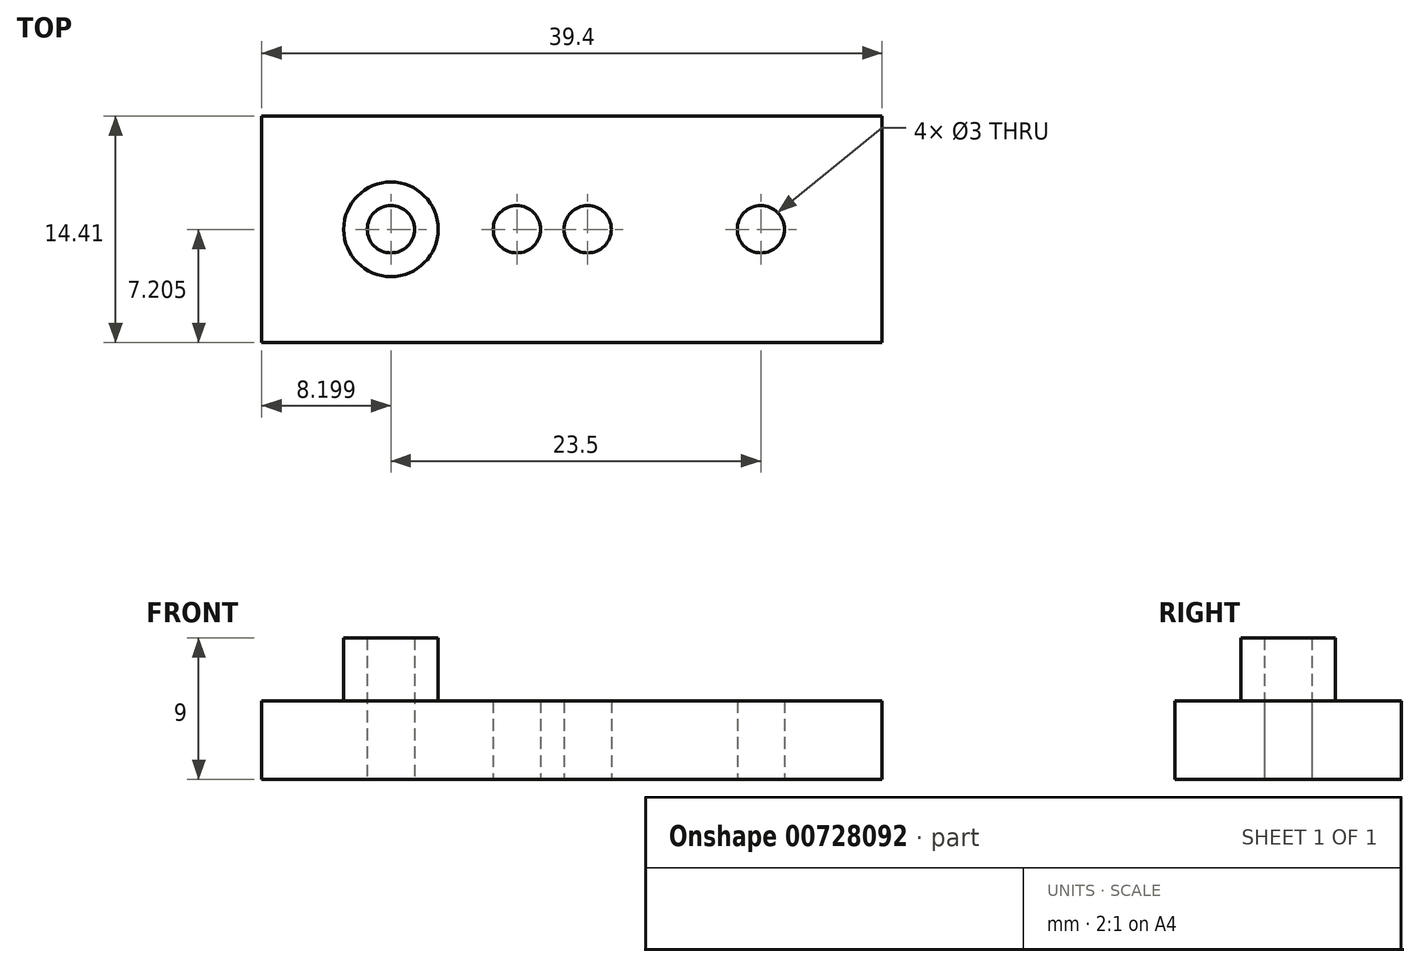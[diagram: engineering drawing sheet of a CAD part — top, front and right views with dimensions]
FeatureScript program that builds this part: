
annotation { "Feature Type Name" : "Feature", "Feature Type Description" : "" }
export const myFeature = defineFeature(function(context is Context, id is Id, definition is map)
    precondition{}
    {
        {
            var Q0;
            Q0=qCreatedBy(makeId("Top.planeOp"),FACE);
            var sketch = newSketch(context, id + "F0", { "sketchPlane" : qUnion([Q0])});
            skLineSegment(sketch, "E0.bottom", {"start": v(0, 0) * mm, "end": v(39.4, 0) * mm});
            skLineSegment(sketch, "E0.top", {"start": v(0, -14.4) * mm, "end": v(39.4, -14.4) * mm});
            skLineSegment(sketch, "E0.left", {"start": v(0, 0) * mm, "end": v(0, -14.4) * mm});
            skLineSegment(sketch, "E0.right", {"start": v(39.4, 0) * mm, "end": v(39.4, -14.4) * mm});
            skCircle(sketch, "E1", {"center": v(20.7, -7.2) * mm, "radius": 1.5 * mm});
            skPoint(sketch, "E1.centerSnap0", {"position": v(0, -7.2) * mm});
            skCircle(sketch, "E2", {"center": v(31.7, -7.2) * mm, "radius": 1.5 * mm});
            skPoint(sketch, "E2.centerSnap0", {"position": v(39.4, -7.2) * mm});
            skCircle(sketch, "E3", {"center": v(16.2, -7.2) * mm, "radius": 1.5 * mm});
            skCircle(sketch, "E4", {"center": v(8.2, -7.2) * mm, "radius": 1.5 * mm});
            skSolve(sketch);
        }
        {
            var Q0;
            Q0=makeQuery(id+"F0.imprint","IMPRINT",FACE,{"disambiguationData":[TD([[makeQuery(id+"F0.imprint","IMPRINT",EDGE,{"derivedFrom":sQuery(id+"F0.wireOp",EDGE,"E0.bottom")}),-1.0]])]});
            extrude(context, id + "F1", {"entities" : qUnion([Q0]), "depth" : 5 * mm, "offsetDistance" : 25 * mm});
        }
        {
            var Q0;
            Q0=makeQuery(id+"F1.opExtrude","CAP_FACE",FACE,{"disambiguationData":[OSD([sQuery(id+"F0.wireOp",EDGE,"E0.bottom"),sQuery(id+"F0.wireOp",EDGE,"E0.top"),sQuery(id+"F0.wireOp",EDGE,"E0.left"),sQuery(id+"F0.wireOp",EDGE,"E0.right"),sQuery(id+"F0.wireOp",EDGE,"E1"),sQuery(id+"F0.wireOp",EDGE,"E2"),sQuery(id+"F0.wireOp",EDGE,"E3"),sQuery(id+"F0.wireOp",EDGE,"E4")])],"isStart":false});
            var sketch = newSketch(context, id + "F2", { "sketchPlane" : qUnion([Q0])});
            skCircle(sketch, "E5", {"center": v(8.2, -7.2) * mm, "radius": 3 * mm});
            skCircle(sketch, "E6", {"center": v(16.2, -7.2) * mm, "radius": 2.75 * mm});
            skSolve(sketch);
        }
        {
            var Q0;
            Q0=makeQuery(id+"F2.imprint","IMPRINT",FACE,{"disambiguationData":[TD([[makeQuery(id+"F2.imprint","IMPRINT",EDGE,{"derivedFrom":sQuery(id+"F2.wireOp",EDGE,"E5")}),1.0]])]});
            extrude(context, id + "F3", {"entities" : qUnion([Q0]), "operationType" : NewBodyOperationType.ADD, "depth" : 4 * mm, "offsetDistance" : 25 * mm});
        }
    });
